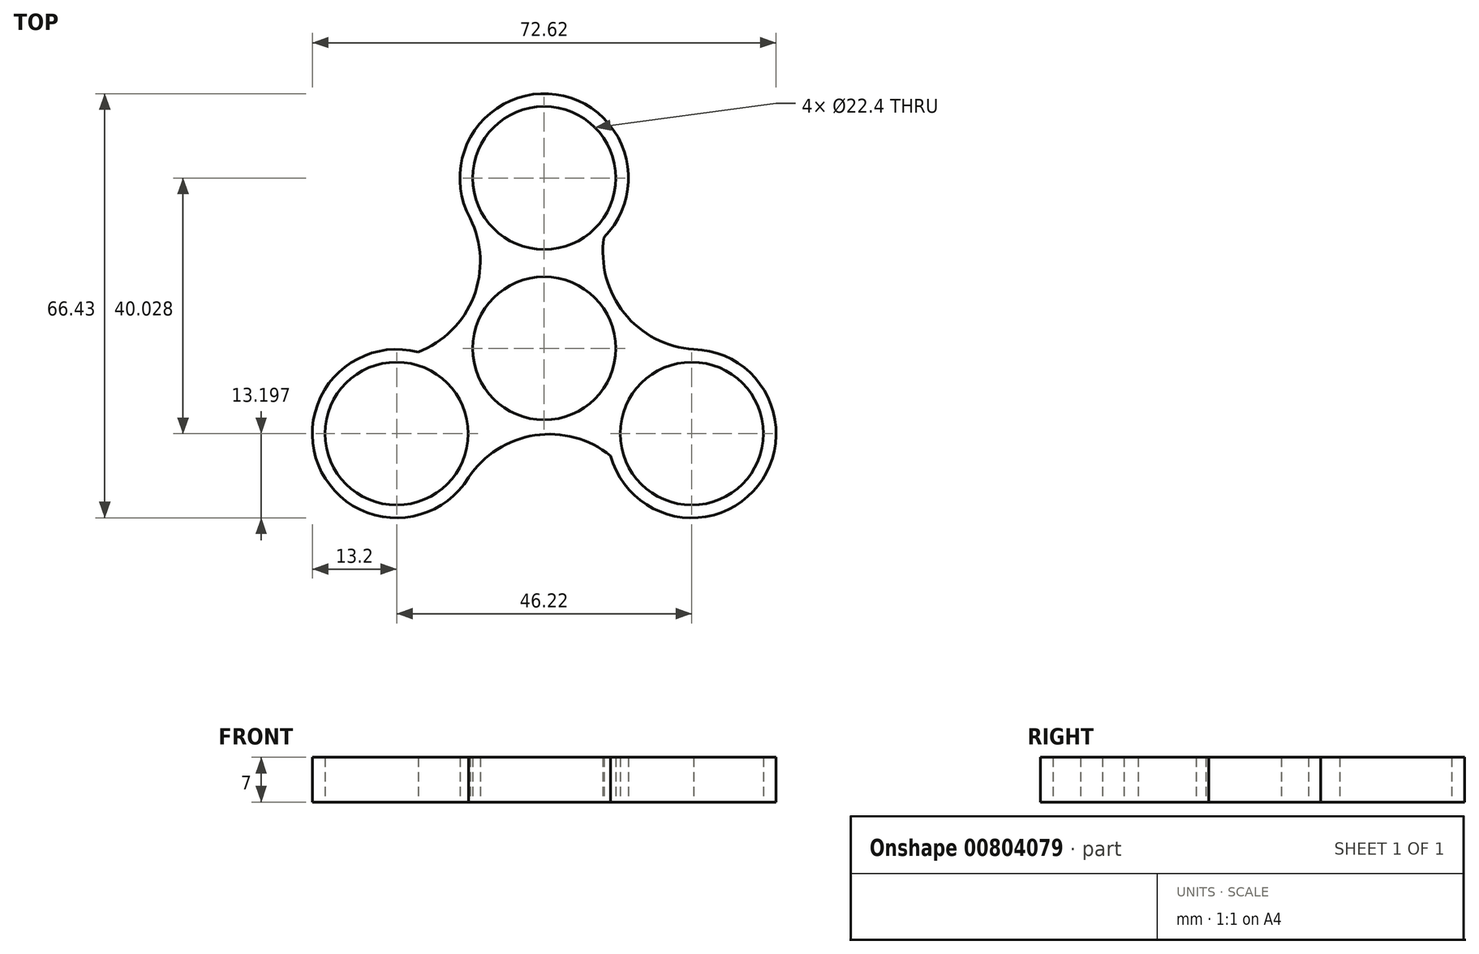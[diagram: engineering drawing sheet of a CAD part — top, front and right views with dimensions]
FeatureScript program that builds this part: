
annotation { "Feature Type Name" : "Feature", "Feature Type Description" : "" }
export const myFeature = defineFeature(function(context is Context, id is Id, definition is map)
    precondition{}
    {
        {
            var Q0;
            Q0=qCreatedBy(makeId("Top.planeOp"),FACE);
            var sketch = newSketch(context, id + "F0", { "sketchPlane" : qUnion([Q0])});
            skCircle(sketch, "E0", {"center": v(0, 0) * mm, "radius": 11.2 * mm});
            skCircle(sketch, "E1", {"center": v(0, 26.69) * mm, "radius": 11.2 * mm});
            skArc(sketch, "E2", {"start": v(9.37, 17.39) * mm, "mid": v(1.85, 39.75) * mm, "end": v(-11.59, 20.36) * mm});
            skCircle(sketch, "E3.1.0", {"center": v(-23.11, -13.34) * mm, "radius": 11.2 * mm});
            skArc(sketch, "E3.1.1", {"start": v(-19.74, -0.58) * mm, "mid": v(-35.35, -18.27) * mm, "end": v(-11.84, -20.21) * mm});
            skCircle(sketch, "E3.2.0", {"center": v(23.11, -13.34) * mm, "radius": 11.2 * mm});
            skArc(sketch, "E3.2.1", {"start": v(10.37, -16.8) * mm, "mid": v(33.5, -21.48) * mm, "end": v(23.42, -0.15) * mm});
            skLineSegment(sketch, "E4", {"start": v(8.85, 6.87) * mm, "end": v(10.85, 8.13) * mm, "construction": true});
            skArc(sketch, "E5", {"start": v(9.37, 17.39) * mm, "mid": v(12.53, 5.52) * mm, "end": v(23.42, -0.15) * mm});
            skArc(sketch, "E6.1.0", {"start": v(-19.74, -0.58) * mm, "mid": v(-11.05, 8.1) * mm, "end": v(-11.59, 20.36) * mm});
            skArc(sketch, "E6.2.0", {"start": v(10.37, -16.8) * mm, "mid": v(-1.48, -13.61) * mm, "end": v(-11.84, -20.21) * mm});
            skSolve(sketch);
        }
        {
            var Q0;
            Q0=makeQuery(id+"F0.imprint","IMPRINT",FACE,{"disambiguationData":[TD([[makeQuery(id+"F0.imprint","IMPRINT",EDGE,{"derivedFrom":sQuery(id+"F0.wireOp",EDGE,"E0")}),-1.0]])]});
            extrude(context, id + "F1", {"entities" : qUnion([Q0]), "depth" : 7 * mm, "offsetDistance" : 25 * mm});
        }
    });
